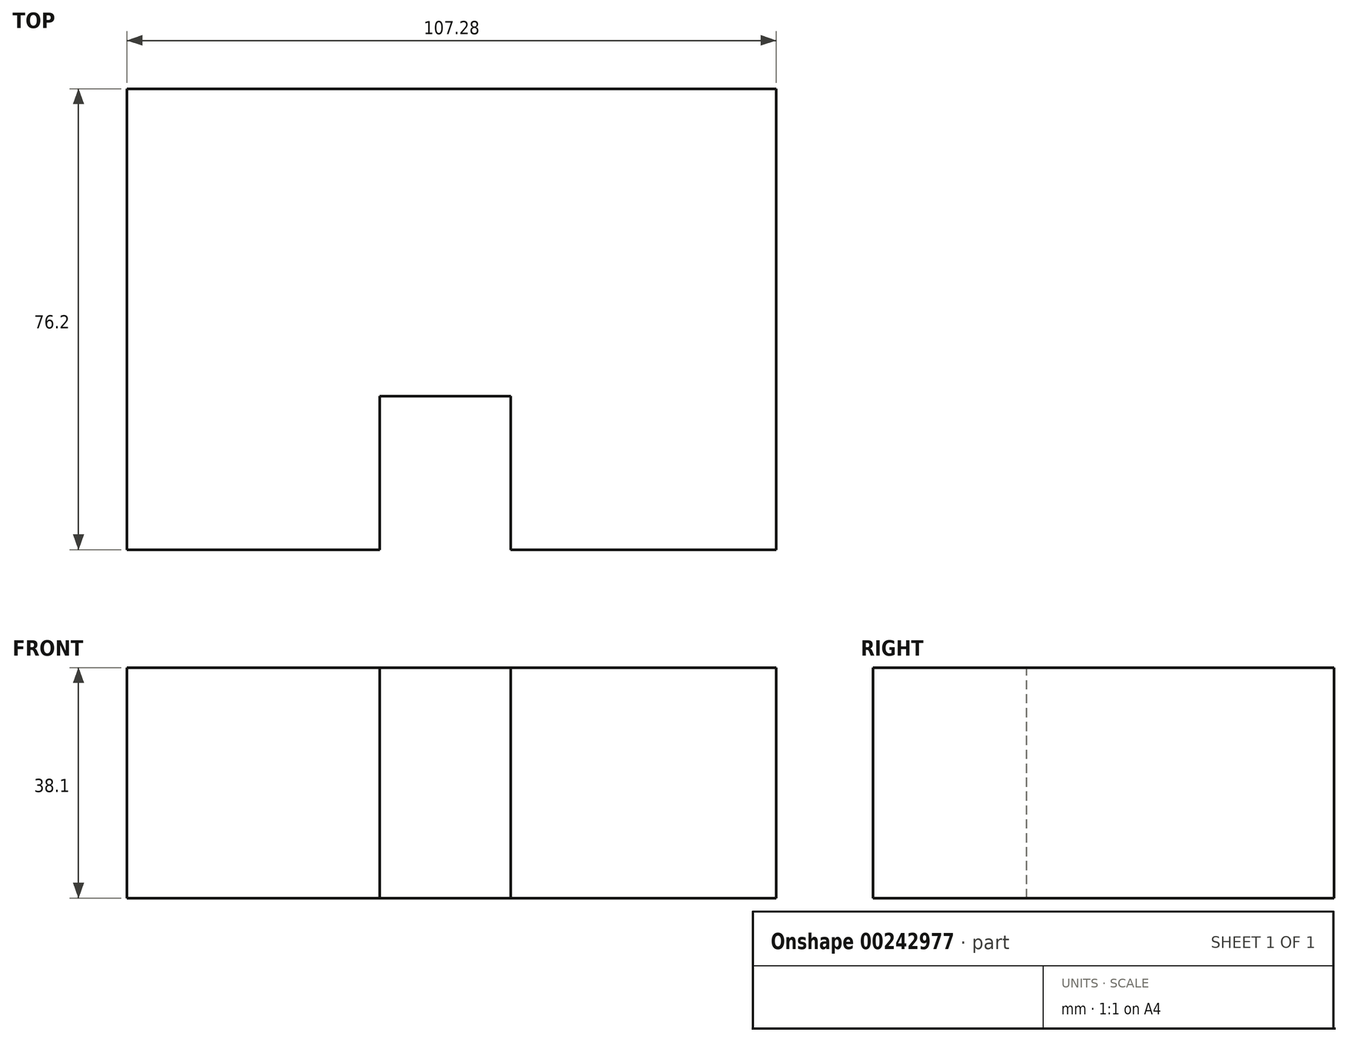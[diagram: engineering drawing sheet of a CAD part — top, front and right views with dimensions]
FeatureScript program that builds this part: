
annotation { "Feature Type Name" : "Feature", "Feature Type Description" : "" }
export const myFeature = defineFeature(function(context is Context, id is Id, definition is map)
    precondition{}
    {
        {
            var Q0;
            Q0=qCreatedBy(makeId("Front.planeOp"),FACE);
            var sketch = newSketch(context, id + "F0", { "sketchPlane" : qUnion([Q0])});
            skLineSegment(sketch, "E0", {"start": v(-76.5, -55.63) * mm, "end": v(-76.5, -17.53) * mm});
            skLineSegment(sketch, "E1", {"start": v(-76.5, -17.53) * mm, "end": v(-35.66, -17.53) * mm});
            skLineSegment(sketch, "E2", {"start": v(-35.66, -17.53) * mm, "end": v(-35.66, -55.63) * mm});
            skLineSegment(sketch, "E3", {"start": v(-35.66, -55.63) * mm, "end": v(-76.5, -55.63) * mm});
            skLineSegment(sketch, "E4", {"start": v(-35.66, -17.53) * mm, "end": v(-10.06, -17.53) * mm});
            skLineSegment(sketch, "E5", {"start": v(-10.06, -17.53) * mm, "end": v(-10.06, -55.63) * mm});
            skLineSegment(sketch, "E6", {"start": v(-10.06, -55.63) * mm, "end": v(-35.66, -55.63) * mm});
            skLineSegment(sketch, "E7", {"start": v(-10.06, -17.53) * mm, "end": v(30.78, -17.53) * mm});
            skLineSegment(sketch, "E8", {"start": v(30.78, -17.53) * mm, "end": v(30.78, -55.63) * mm});
            skLineSegment(sketch, "E9", {"start": v(30.78, -55.63) * mm, "end": v(-10.06, -55.63) * mm});
            skLineSegment(sketch, "E10", {"start": v(-76.5, -17.53) * mm, "end": v(-76.5, 55.02) * mm});
            skLineSegment(sketch, "E11", {"start": v(-76.5, 55.02) * mm, "end": v(-61.26, 55.02) * mm});
            skLineSegment(sketch, "E12", {"start": v(-61.26, 55.02) * mm, "end": v(-61.26, 29.41) * mm});
            skLineSegment(sketch, "E13", {"start": v(-61.26, 29.41) * mm, "end": v(16.76, 29.41) * mm});
            skLineSegment(sketch, "E14", {"start": v(16.76, 29.41) * mm, "end": v(16.76, 55.02) * mm});
            skLineSegment(sketch, "E15", {"start": v(16.76, 55.02) * mm, "end": v(30.78, 55.02) * mm});
            skLineSegment(sketch, "E16", {"start": v(30.78, 55.02) * mm, "end": v(30.78, -17.53) * mm});
            skSolve(sketch);
        }
        {
            var Q0;
            Q0=makeQuery(id+"F0.imprint","IMPRINT",FACE,{"disambiguationData":[TD([[makeQuery(id+"F0.imprint","IMPRINT",EDGE,{"derivedFrom":sQuery(id+"F0.wireOp",EDGE,"E0")}),-1.0]])]});
            var Q1;
            Q1=makeQuery(id+"F0.imprint","IMPRINT",FACE,{"disambiguationData":[TD([[makeQuery(id+"F0.imprint","IMPRINT",EDGE,{"derivedFrom":sQuery(id+"F0.wireOp",EDGE,"E2")}),1.0]])]});
            var Q2;
            Q2=makeQuery(id+"F0.imprint","IMPRINT",FACE,{"disambiguationData":[TD([[makeQuery(id+"F0.imprint","IMPRINT",EDGE,{"derivedFrom":sQuery(id+"F0.wireOp",EDGE,"E5")}),1.0]])]});
            extrude(context, id + "F1", {"entities" : qUnion([Q0, Q1, Q2]), "depth" : 76.2 * mm});
        }
        {
            var Q0;
            Q0=makeQuery(id+"F1.opExtrude","CAP_FACE",FACE,{"disambiguationData":[OSD([sQuery(id+"F0.wireOp",EDGE,"E0"),sQuery(id+"F0.wireOp",EDGE,"E3"),sQuery(id+"F0.wireOp",EDGE,"E6"),sQuery(id+"F0.wireOp",EDGE,"E8"),sQuery(id+"F0.wireOp",EDGE,"E9"),sQuery(id+"F0.wireOp",EDGE,"E10"),sQuery(id+"F0.wireOp",EDGE,"E11"),sQuery(id+"F0.wireOp",EDGE,"E12"),sQuery(id+"F0.wireOp",EDGE,"E13"),sQuery(id+"F0.wireOp",EDGE,"E14"),sQuery(id+"F0.wireOp",EDGE,"E15"),sQuery(id+"F0.wireOp",EDGE,"E16")])],"isStart":false});
            var sketch = newSketch(context, id + "F2", { "sketchPlane" : qUnion([Q0])});
            skLineSegment(sketch, "E17.bottom", {"start": v(-34.75, -55.63) * mm, "end": v(-13.1, -55.63) * mm});
            skLineSegment(sketch, "E17.top", {"start": v(-34.75, -17.53) * mm, "end": v(-13.1, -17.53) * mm});
            skLineSegment(sketch, "E17.left", {"start": v(-34.75, -55.63) * mm, "end": v(-34.75, -17.53) * mm});
            skLineSegment(sketch, "E17.right", {"start": v(-13.1, -55.63) * mm, "end": v(-13.1, -17.53) * mm});
            skSolve(sketch);
        }
        {
            var Q0;
            Q0=makeQuery(id+"F2.imprint","IMPRINT",FACE,{"disambiguationData":[TD([[makeQuery(id+"F2.imprint","IMPRINT",EDGE,{"derivedFrom":sQuery(id+"F2.wireOp",EDGE,"E17.bottom")}),-1.0]])]});
            extrude(context, id + "F3", {"entities" : qUnion([Q0]), "operationType" : NewBodyOperationType.REMOVE, "oppositeDirection" : true, "depth" : 25.4 * mm});
        }
    });
